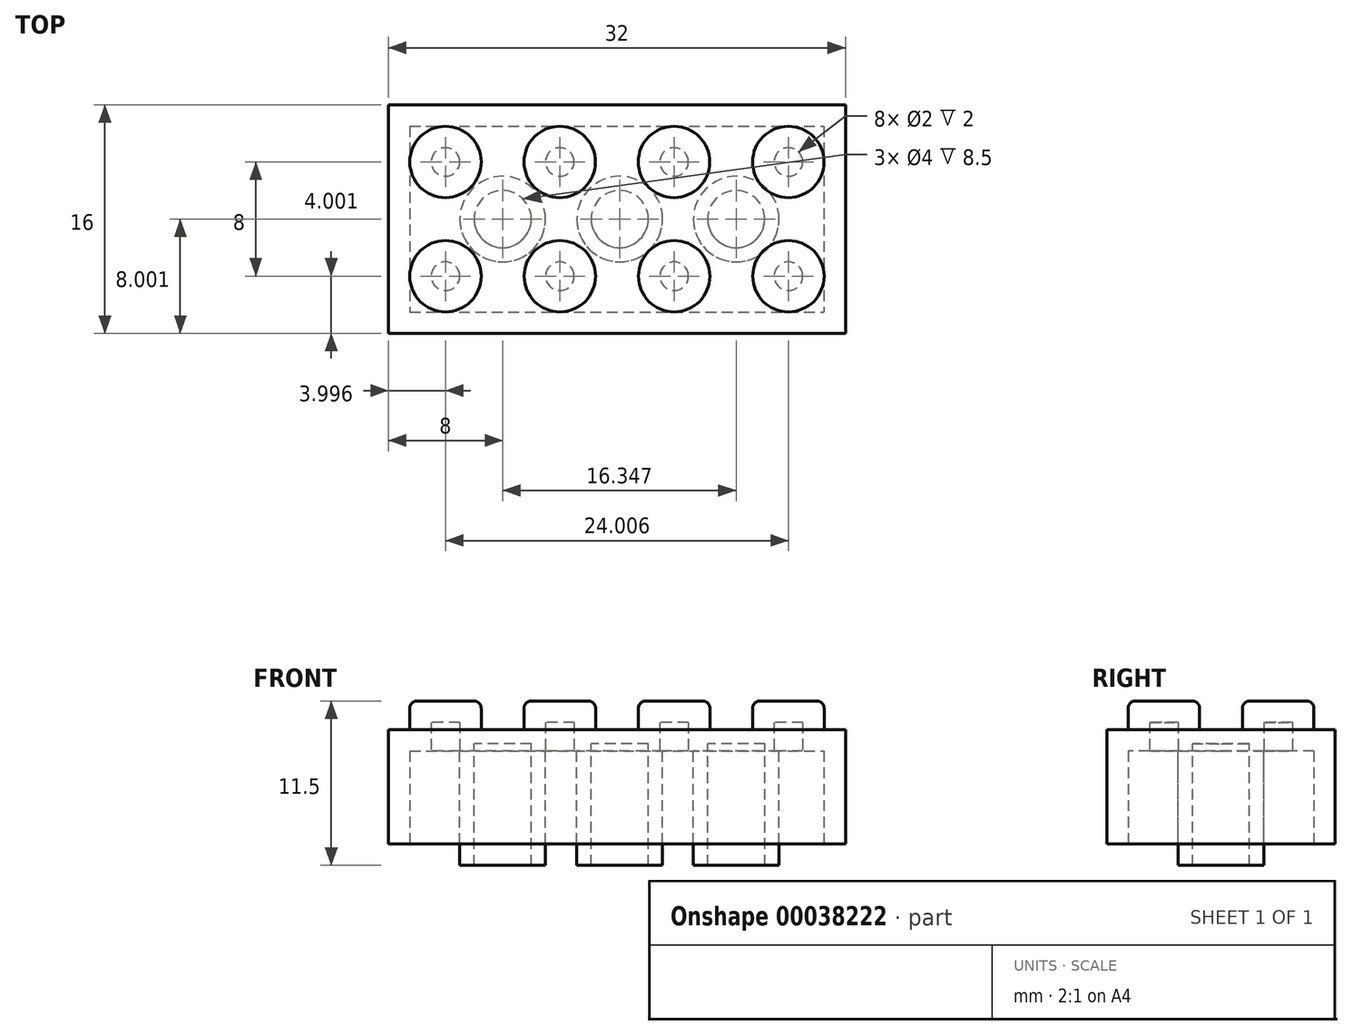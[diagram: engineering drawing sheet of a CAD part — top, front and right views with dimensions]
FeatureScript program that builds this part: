
annotation { "Feature Type Name" : "Feature", "Feature Type Description" : "" }
export const myFeature = defineFeature(function(context is Context, id is Id, definition is map)
    precondition{}
    {
        {
            var Q0;
            Q0=qCreatedBy(makeId("Top.planeOp"),FACE);
            var sketch = newSketch(context, id + "F0", { "sketchPlane" : qUnion([Q0])});
            skLineSegment(sketch, "E0.bottom", {"start": v(-17.4, 9.43) * mm, "end": v(14.6, 9.43) * mm});
            skLineSegment(sketch, "E0.top", {"start": v(-17.4, -6.57) * mm, "end": v(14.6, -6.57) * mm});
            skLineSegment(sketch, "E0.left", {"start": v(-17.4, 9.43) * mm, "end": v(-17.4, -6.57) * mm});
            skLineSegment(sketch, "E0.right", {"start": v(14.6, 9.43) * mm, "end": v(14.6, -6.57) * mm});
            skSolve(sketch);
        }
        {
            var Q0;
            Q0 = qSketchRegion(id + "F0", true);
            extrude(context, id + "F1", {"entities" : qUnion([Q0]), "depth" : 8 * mm});
        }
        {
            var Q0;
            Q0=makeQuery(id+"F1.opExtrude","CAP_FACE",FACE,{"disambiguationData":[OSD([sQuery(id+"F0.wireOp",EDGE,"E0.bottom"),sQuery(id+"F0.wireOp",EDGE,"E0.top"),sQuery(id+"F0.wireOp",EDGE,"E0.left"),sQuery(id+"F0.wireOp",EDGE,"E0.right")])],"isStart":false});
            var sketch = newSketch(context, id + "F2", { "sketchPlane" : qUnion([Q0])});
            skCircle(sketch, "E1", {"center": v(-13.4, 5.43) * mm, "radius": 2.5 * mm});
            skCircle(sketch, "E2", {"center": v(-5.4, 5.43) * mm, "radius": 2.5 * mm});
            skCircle(sketch, "E3", {"center": v(2.6, 5.43) * mm, "radius": 2.5 * mm});
            skCircle(sketch, "E4", {"center": v(10.6, 5.43) * mm, "radius": 2.5 * mm});
            skCircle(sketch, "E5", {"center": v(-13.4, -2.57) * mm, "radius": 2.5 * mm});
            skCircle(sketch, "E6", {"center": v(-5.4, -2.57) * mm, "radius": 2.5 * mm});
            skCircle(sketch, "E7", {"center": v(2.6, -2.57) * mm, "radius": 2.5 * mm});
            skCircle(sketch, "E8", {"center": v(10.6, -2.57) * mm, "radius": 2.5 * mm});
            skSolve(sketch);
        }
        {
            var Q0;
            Q0 = qSketchRegion(id + "F2", true);
            extrude(context, id + "F3", {"entities" : qUnion([Q0]), "operationType" : NewBodyOperationType.ADD, "depth" : 2 * mm});
        }
        {
            var Q0;
            Q0=makeQuery(id+"F3.opExtrude","CAP_FACE",FACE,{"disambiguationData":[OSD([sQuery(id+"F2.wireOp",EDGE,"E8")])],"isStart":false});
            var Q1;
            Q1=makeQuery(id+"F3.opExtrude","CAP_FACE",FACE,{"disambiguationData":[OSD([sQuery(id+"F2.wireOp",EDGE,"E4")])],"isStart":false});
            var Q2;
            Q2=makeQuery(id+"F3.opExtrude","CAP_FACE",FACE,{"disambiguationData":[OSD([sQuery(id+"F2.wireOp",EDGE,"E5")])],"isStart":false});
            var Q3;
            Q3=makeQuery(id+"F3.opExtrude","CAP_FACE",FACE,{"disambiguationData":[OSD([sQuery(id+"F2.wireOp",EDGE,"E6")])],"isStart":false});
            var Q4;
            Q4=makeQuery(id+"F3.opExtrude","CAP_FACE",FACE,{"disambiguationData":[OSD([sQuery(id+"F2.wireOp",EDGE,"E7")])],"isStart":false});
            var Q5;
            Q5=makeQuery(id+"F3.opExtrude","CAP_FACE",FACE,{"disambiguationData":[OSD([sQuery(id+"F2.wireOp",EDGE,"E3")])],"isStart":false});
            var Q6;
            Q6=makeQuery(id+"F3.opExtrude","CAP_FACE",FACE,{"disambiguationData":[OSD([sQuery(id+"F2.wireOp",EDGE,"E2")])],"isStart":false});
            var Q7;
            Q7=makeQuery(id+"F3.opExtrude","CAP_FACE",FACE,{"disambiguationData":[OSD([sQuery(id+"F2.wireOp",EDGE,"E1")])],"isStart":false});
            fillet(context, id + "F4", {"entities" : qUnion([Q0, Q1, Q2, Q3, Q4, Q5, Q6, Q7]), "radius" : 0.5 * mm, "tangentPropagation" : true, "allowEdgeOverflow" : false});
        }
        {
            var Q0;
            Q0=makeQuery(id+"F1.opExtrude","CAP_FACE",FACE,{"disambiguationData":[OSD([sQuery(id+"F0.wireOp",EDGE,"E0.bottom"),sQuery(id+"F0.wireOp",EDGE,"E0.top"),sQuery(id+"F0.wireOp",EDGE,"E0.left"),sQuery(id+"F0.wireOp",EDGE,"E0.right")])],"isStart":true});
            shell(context, id + "F5", {"entities" : qUnion([Q0]), "thickness" : 1.5 * mm});
        }
        {
            var Q0;
            Q0=makeQuery(id+"F5.opShell","OFFSET_FACE",FACE,{"disambiguationData":[OSD([sQuery(id+"F0.wireOp",EDGE,"E0.bottom"),sQuery(id+"F0.wireOp",EDGE,"E0.top"),sQuery(id+"F0.wireOp",EDGE,"E0.left"),sQuery(id+"F0.wireOp",EDGE,"E0.right")])]});
            var sketch = newSketch(context, id + "F6", { "sketchPlane" : qUnion([Q0])});
            skPoint(sketch, "E9.startSnap0", {"position": v(-15.9, -1.43) * mm});
            skCircle(sketch, "E10", {"center": v(-9.4, -1.43) * mm, "radius": 3 * mm});
            skCircle(sketch, "E11", {"center": v(-1.2, -1.43) * mm, "radius": 3 * mm});
            skCircle(sketch, "E12", {"center": v(6.95, -1.43) * mm, "radius": 3 * mm});
            skSolve(sketch);
        }
        {
            var Q0;
            Q0=makeQuery(id+"F6.imprint","IMPRINT",FACE,{"disambiguationData":[TD([[makeQuery(id+"F6.imprint","IMPRINT",EDGE,{"derivedFrom":sQuery(id+"F6.wireOp",EDGE,"E10")}),1.0]])]});
            var Q1;
            Q1=makeQuery(id+"F6.imprint","IMPRINT",FACE,{"disambiguationData":[TD([[makeQuery(id+"F6.imprint","IMPRINT",EDGE,{"derivedFrom":sQuery(id+"F6.wireOp",EDGE,"E11")}),1.0]])]});
            var Q2;
            Q2=makeQuery(id+"F6.imprint","IMPRINT",FACE,{"disambiguationData":[TD([[makeQuery(id+"F6.imprint","IMPRINT",EDGE,{"derivedFrom":sQuery(id+"F6.wireOp",EDGE,"E12")}),1.0]])]});
            extrude(context, id + "F7", {"entities" : qUnion([Q0, Q1, Q2]), "operationType" : NewBodyOperationType.ADD, "depth" : 8 * mm});
        }
        {
            var Q0;
            Q0=makeQuery(id+"F7.opExtrude","CAP_FACE",FACE,{"disambiguationData":[OSD([sQuery(id+"F6.wireOp",EDGE,"E10")])],"isStart":false});
            var Q1;
            Q1=makeQuery(id+"F7.opExtrude","CAP_FACE",FACE,{"disambiguationData":[OSD([sQuery(id+"F6.wireOp",EDGE,"E11")])],"isStart":false});
            var Q2;
            Q2=makeQuery(id+"F7.opExtrude","CAP_FACE",FACE,{"disambiguationData":[OSD([sQuery(id+"F6.wireOp",EDGE,"E12")])],"isStart":false});
            shell(context, id + "F8", {"entities" : qUnion([Q0, Q1, Q2]), "thickness" : 1 * mm});
        }
    });
